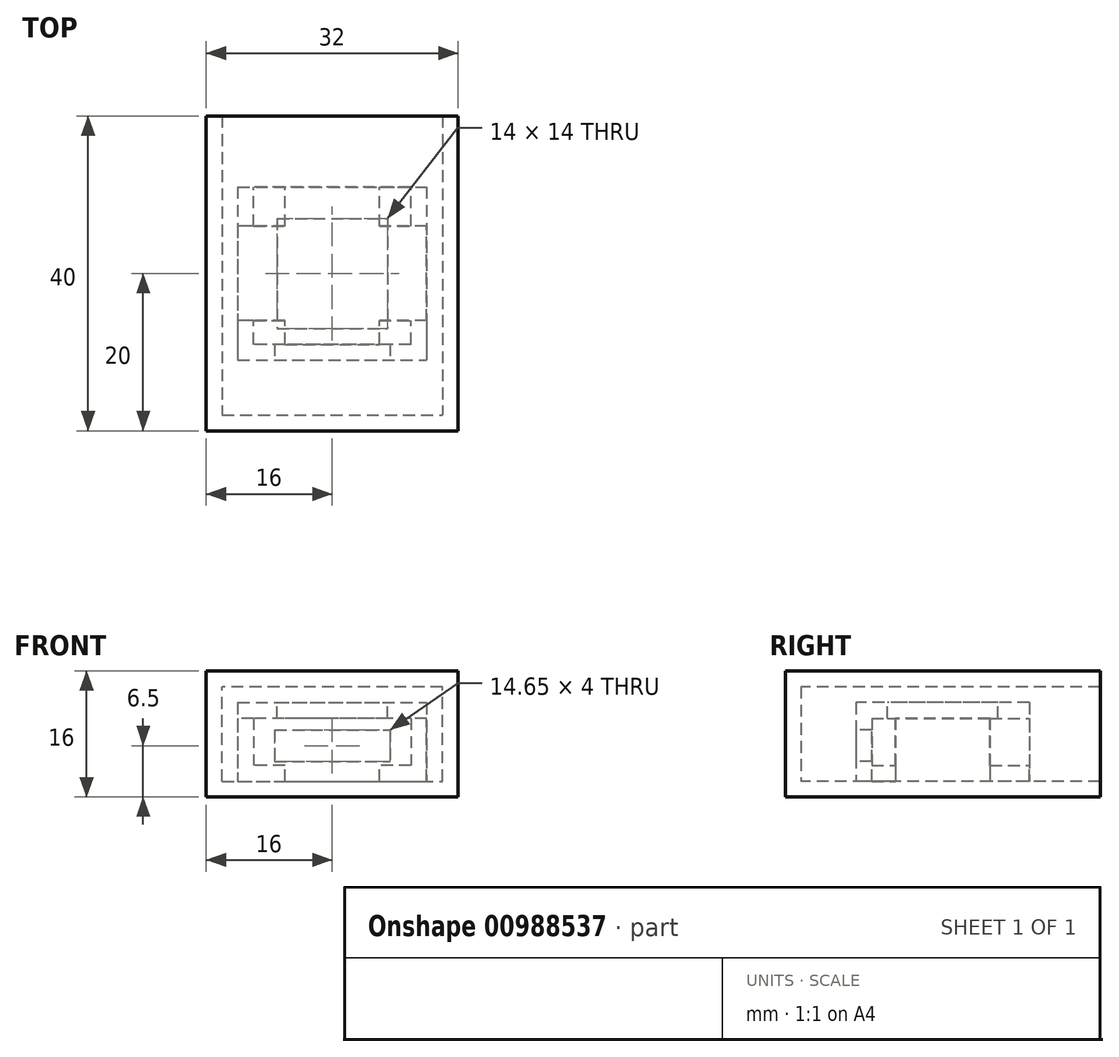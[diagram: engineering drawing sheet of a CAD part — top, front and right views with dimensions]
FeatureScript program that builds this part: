
annotation { "Feature Type Name" : "Feature", "Feature Type Description" : "" }
export const myFeature = defineFeature(function(context is Context, id is Id, definition is map)
    precondition{}
    {
        {
            var Q0;
            Q0=qCreatedBy(makeId("Top.planeOp"),FACE);
            var sketch = newSketch(context, id + "F0", { "sketchPlane" : qUnion([Q0])});
            skLineSegment(sketch, "E0.bottom", {"start": v(-16, 20) * mm, "end": v(16, 20) * mm});
            skLineSegment(sketch, "E0.top", {"start": v(-16, -20) * mm, "end": v(16, -20) * mm});
            skLineSegment(sketch, "E0.left", {"start": v(-16, 20) * mm, "end": v(-16, -20) * mm});
            skLineSegment(sketch, "E0.right", {"start": v(16, 20) * mm, "end": v(16, -20) * mm});
            skPoint(sketch, "E0.middle", {"position": v(0, 0) * mm});
            skSolve(sketch);
        }
        {
            var Q0;
            Q0=makeQuery(id+"F0.imprint","IMPRINT",FACE,{"disambiguationData":[TD([[makeQuery(id+"F0.imprint","IMPRINT",EDGE,{"derivedFrom":sQuery(id+"F0.wireOp",EDGE,"E0.bottom")}),-1.0]])]});
            extrude(context, id + "F1", {"entities" : qUnion([Q0]), "depth" : 2 * mm, "offsetDistance" : 25 * mm});
        }
        {
            var Q0;
            Q0=makeQuery(id+"F1.opExtrude","CAP_FACE",FACE,{"disambiguationData":[OSD([sQuery(id+"F0.wireOp",EDGE,"E0.bottom"),sQuery(id+"F0.wireOp",EDGE,"E0.top"),sQuery(id+"F0.wireOp",EDGE,"E0.left"),sQuery(id+"F0.wireOp",EDGE,"E0.right")])],"isStart":false});
            var sketch = newSketch(context, id + "F2", { "sketchPlane" : qUnion([Q0])});
            skLineSegment(sketch, "E1.bottom", {"start": v(-14, 18) * mm, "end": v(14, 18) * mm});
            skLineSegment(sketch, "E1.top", {"start": v(-14, -18) * mm, "end": v(14, -18) * mm});
            skLineSegment(sketch, "E1.left", {"start": v(-14, 18) * mm, "end": v(-14, -18) * mm});
            skLineSegment(sketch, "E1.right", {"start": v(14, 18) * mm, "end": v(14, -18) * mm});
            skPoint(sketch, "E1.middle", {"position": v(0, 0) * mm});
            skSolve(sketch);
        }
        {
            var Q0;
            Q0=makeQuery(id+"F2.imprint","IMPRINT",FACE,{"disambiguationData":[TD([[makeQuery(id+"F2.imprint","IMPRINT",EDGE,{"derivedFrom":sQuery(id+"F2.wireOp",EDGE,"E1.bottom")}),-1.0]])]});
            var sketch = newSketch(context, id + "F3", { "sketchPlane" : qUnion([Q0])});
            skLineSegment(sketch, "E2.bottom", {"start": v(-11, 11) * mm, "end": v(11, 11) * mm});
            skLineSegment(sketch, "E2.top", {"start": v(-11, -11) * mm, "end": v(11, -11) * mm});
            skLineSegment(sketch, "E2.left", {"start": v(-11, 11) * mm, "end": v(-11, -11) * mm});
            skLineSegment(sketch, "E2.right", {"start": v(11, 11) * mm, "end": v(11, -11) * mm});
            skPoint(sketch, "E2.middle", {"position": v(0, 0) * mm});
            skSolve(sketch);
        }
        {
            var Q0;
            Q0=makeQuery(id+"F3.imprint","IMPRINT",FACE,{"disambiguationData":[TD([[makeQuery(id+"F3.imprint","IMPRINT",EDGE,{"derivedFrom":sQuery(id+"F3.wireOp",EDGE,"E2.bottom")}),-1.0]])]});
            extrude(context, id + "F4", {"entities" : qUnion([Q0]), "operationType" : NewBodyOperationType.ADD, "depth" : 10 * mm, "offsetDistance" : 25 * mm});
        }
        {
            var Q0;
            Q0=makeQuery(id+"F4.opExtrude","SWEPT_FACE",FACE,{"disambiguationData":[OSD([sQuery(id+"F3.wireOp",EDGE,"E2.bottom")])]});
            var sketch = newSketch(context, id + "F5", { "sketchPlane" : qUnion([Q0])});
            skPoint(sketch, "E3", {"position": v(0, 7) * mm});
            skPoint(sketch, "E3.positionSnap0", {"position": v(0, 2) * mm});
            skLineSegment(sketch, "E4.bottom", {"start": v(-10, 10) * mm, "end": v(10, 10) * mm});
            skLineSegment(sketch, "E4.top", {"start": v(-10, 4) * mm, "end": v(10, 4) * mm});
            skLineSegment(sketch, "E4.left", {"start": v(-10, 10) * mm, "end": v(-10, 4) * mm});
            skLineSegment(sketch, "E4.right", {"start": v(10, 10) * mm, "end": v(10, 4) * mm});
            skSolve(sketch);
        }
        {
            var Q0;
            Q0=makeQuery(id+"F4.opExtrude","SWEPT_FACE",FACE,{"disambiguationData":[OSD([sQuery(id+"F3.wireOp",EDGE,"E2.left")])]});
            extrude(context, id + "F6", {"entities" : qUnion([Q0]), "operationType" : NewBodyOperationType.ADD, "depth" : 1 * mm, "offsetDistance" : 25 * mm});
        }
        {
            var Q0;
            Q0=makeQuery(id+"F4.opExtrude","SWEPT_FACE",FACE,{"disambiguationData":[OSD([sQuery(id+"F3.wireOp",EDGE,"E2.right")])]});
            extrude(context, id + "F7", {"entities" : qUnion([Q0]), "operationType" : NewBodyOperationType.ADD, "depth" : 1 * mm, "offsetDistance" : 25 * mm});
        }
        {
            var Q0;
            Q0=makeQuery(id+"F5.imprint","IMPRINT",FACE,{"disambiguationData":[TD([[makeQuery(id+"F5.imprint","IMPRINT",EDGE,{"derivedFrom":sQuery(id+"F5.wireOp",EDGE,"E4.bottom")}),-1.0]])]});
            extrude(context, id + "F8", {"entities" : qUnion([Q0]), "operationType" : NewBodyOperationType.REMOVE, "oppositeDirection" : true, "depth" : 20 * mm, "offsetDistance" : 25 * mm});
        }
        {
            var Q0;
            {var subQ0=sQuery(id+"F3.wireOp",EDGE,"E2.bottom");Q0=makeQuery(id+"F7.boolean.opBoolean","MERGE",FACE,{"derivedFrom":[makeQuery(id+"F6.boolean.opBoolean","MERGE",FACE,{"derivedFrom":[makeQuery(id+"F4.opExtrude","SWEPT_FACE",FACE,{"disambiguationData":[OSD([subQ0])]}),makeQuery(id+"F6.opExtrude","SWEPT_FACE",FACE,{"disambiguationData":[OSD([subQ0,sQuery(id+"F3.wireOp",EDGE,"E2.left")])]})]}),makeQuery(id+"F7.opExtrude","SWEPT_FACE",FACE,{"disambiguationData":[OSD([subQ0,sQuery(id+"F3.wireOp",EDGE,"E2.right")])]})]});}
            var sketch = newSketch(context, id + "F9", { "sketchPlane" : qUnion([Q0])});
            skPoint(sketch, "E5", {"position": v(0, 3) * mm});
            skPoint(sketch, "E5.positionSnap0", {"position": v(0, 2) * mm});
            skLineSegment(sketch, "E6.bottom", {"start": v(-6, 2) * mm, "end": v(6, 2) * mm});
            skLineSegment(sketch, "E6.top", {"start": v(-6, 4) * mm, "end": v(6, 4) * mm});
            skLineSegment(sketch, "E6.left", {"start": v(-6, 2) * mm, "end": v(-6, 4) * mm});
            skLineSegment(sketch, "E6.right", {"start": v(6, 2) * mm, "end": v(6, 4) * mm});
            skSolve(sketch);
        }
        {
            var Q0;
            Q0=makeQuery(id+"F9.imprint","IMPRINT",FACE,{"disambiguationData":[TD([[makeQuery(id+"F9.imprint","IMPRINT",EDGE,{"derivedFrom":sQuery(id+"F9.wireOp",EDGE,"E6.bottom")}),-1.0]])]});
            extrude(context, id + "F10", {"entities" : qUnion([Q0]), "operationType" : NewBodyOperationType.REMOVE, "oppositeDirection" : true, "depth" : 20 * mm, "offsetDistance" : 25 * mm});
        }
        {
            var Q0;
            Q0=makeQuery(id+"F6.opExtrude","CAP_FACE",FACE,{"disambiguationData":[OSD([sQuery(id+"F3.wireOp",EDGE,"E2.left")])],"isStart":false});
            var sketch = newSketch(context, id + "F11", { "sketchPlane" : qUnion([Q0])});
            skPoint(sketch, "E7", {"position": v(0, 6) * mm});
            skPoint(sketch, "E7.positionSnap0", {"position": v(0, 2) * mm});
            skLineSegment(sketch, "E8.bottom", {"start": v(-6, 10) * mm, "end": v(6, 10) * mm});
            skLineSegment(sketch, "E8.top", {"start": v(-6, 2) * mm, "end": v(6, 2) * mm});
            skLineSegment(sketch, "E8.left", {"start": v(-6, 10) * mm, "end": v(-6, 2) * mm});
            skLineSegment(sketch, "E8.right", {"start": v(6, 10) * mm, "end": v(6, 2) * mm});
            skSolve(sketch);
        }
        {
            var Q0;
            Q0=makeQuery(id+"F11.imprint","IMPRINT",FACE,{"disambiguationData":[TD([[makeQuery(id+"F11.imprint","IMPRINT",EDGE,{"derivedFrom":sQuery(id+"F11.wireOp",EDGE,"E8.bottom")}),-1.0]])]});
            extrude(context, id + "F12", {"entities" : qUnion([Q0]), "operationType" : NewBodyOperationType.REMOVE, "oppositeDirection" : true, "depth" : 25 * mm, "offsetDistance" : 25 * mm});
        }
        {
            var Q0;
            {var subQ0=sQuery(id+"F3.wireOp",EDGE,"E2.top");Q0=makeQuery(id+"F7.boolean.opBoolean","MERGE",FACE,{"derivedFrom":[makeQuery(id+"F6.boolean.opBoolean","MERGE",FACE,{"derivedFrom":[makeQuery(id+"F4.opExtrude","SWEPT_FACE",FACE,{"disambiguationData":[OSD([subQ0])]}),makeQuery(id+"F6.opExtrude","SWEPT_FACE",FACE,{"disambiguationData":[OSD([subQ0,sQuery(id+"F3.wireOp",EDGE,"E2.left")])]})]}),makeQuery(id+"F7.opExtrude","SWEPT_FACE",FACE,{"disambiguationData":[OSD([subQ0,sQuery(id+"F3.wireOp",EDGE,"E2.right")])]})]});}
            var sketch = newSketch(context, id + "F13", { "sketchPlane" : qUnion([Q0])});
            skPoint(sketch, "E9", {"position": v(0, 6.5) * mm});
            skPoint(sketch, "E9.positionSnap0", {"position": v(0, 2) * mm});
            skLineSegment(sketch, "E10.bottom", {"start": v(-7.32, 8.5) * mm, "end": v(7.32, 8.5) * mm});
            skLineSegment(sketch, "E10.top", {"start": v(-7.32, 4.5) * mm, "end": v(7.32, 4.5) * mm});
            skLineSegment(sketch, "E10.left", {"start": v(-7.32, 8.5) * mm, "end": v(-7.32, 4.5) * mm});
            skLineSegment(sketch, "E10.right", {"start": v(7.32, 8.5) * mm, "end": v(7.32, 4.5) * mm});
            skSolve(sketch);
        }
        {
            var Q0;
            Q0=makeQuery(id+"F13.imprint","IMPRINT",FACE,{"disambiguationData":[TD([[makeQuery(id+"F13.imprint","IMPRINT",EDGE,{"derivedFrom":sQuery(id+"F13.wireOp",EDGE,"E10.bottom")}),-1.0]])]});
            extrude(context, id + "F14", {"entities" : qUnion([Q0]), "operationType" : NewBodyOperationType.REMOVE, "oppositeDirection" : true, "depth" : 25 * mm, "offsetDistance" : 25 * mm});
        }
        {
            var Q0;
            {var subQ0=sQuery(id+"F3.wireOp",EDGE,"E2.right");var subQ1=sQuery(id+"F3.wireOp",EDGE,"E2.left");Q0=makeQuery(id+"F7.boolean.opBoolean","MERGE",FACE,{"derivedFrom":[makeQuery(id+"F6.boolean.opBoolean","MERGE",FACE,{"derivedFrom":[makeQuery(id+"F4.opExtrude","CAP_FACE",FACE,{"disambiguationData":[OSD([sQuery(id+"F3.wireOp",EDGE,"E2.bottom"),sQuery(id+"F3.wireOp",EDGE,"E2.top"),subQ1,subQ0])],"isStart":false}),makeQuery(id+"F6.opExtrude","SWEPT_FACE",FACE,{"disambiguationData":[OSD([subQ1]),TDD([makeQuery(id+"F4.opExtrude","CAP_EDGE",EDGE,{"disambiguationData":[OSD([subQ1])],"isStart":false})])]})]}),makeQuery(id+"F7.opExtrude","SWEPT_FACE",FACE,{"disambiguationData":[OSD([subQ0]),TDD([makeQuery(id+"F4.opExtrude","CAP_EDGE",EDGE,{"disambiguationData":[OSD([subQ0])],"isStart":false})])]})]});}
            var sketch = newSketch(context, id + "F15", { "sketchPlane" : qUnion([Q0])});
            skLineSegment(sketch, "E11.bottom", {"start": v(-7, 7) * mm, "end": v(7, 7) * mm});
            skLineSegment(sketch, "E11.top", {"start": v(-7, -7) * mm, "end": v(7, -7) * mm});
            skLineSegment(sketch, "E11.left", {"start": v(-7, 7) * mm, "end": v(-7, -7) * mm});
            skLineSegment(sketch, "E11.right", {"start": v(7, 7) * mm, "end": v(7, -7) * mm});
            skPoint(sketch, "E11.middle", {"position": v(0, 0) * mm});
            skSolve(sketch);
        }
        {
            var Q0;
            Q0=makeQuery(id+"F15.imprint","IMPRINT",FACE,{"disambiguationData":[TD([[makeQuery(id+"F15.imprint","IMPRINT",EDGE,{"derivedFrom":sQuery(id+"F15.wireOp",EDGE,"E11.bottom")}),-1.0]])]});
            extrude(context, id + "F16", {"entities" : qUnion([Q0]), "operationType" : NewBodyOperationType.REMOVE, "oppositeDirection" : true, "depth" : 5 * mm, "offsetDistance" : 25 * mm});
        }
        {
            var Q0;
            Q0=makeQuery(id+"F2.imprint","IMPRINT",FACE,{"disambiguationData":[TD([[makeQuery(id+"F2.imprint","IMPRINT",EDGE,{"derivedFrom":sQuery(id+"F2.wireOp",EDGE,"E1.bottom")}),1.0]])]});
            extrude(context, id + "F17", {"entities" : qUnion([Q0]), "operationType" : NewBodyOperationType.ADD, "depth" : 14 * mm, "offsetDistance" : 25 * mm});
        }
        {
            var Q0;
            Q0=makeQuery(id+"F17.opExtrude","SWEPT_FACE",FACE,{"disambiguationData":[OSD([sQuery(id+"F2.wireOp",EDGE,"E1.top")])]});
            var sketch = newSketch(context, id + "F18", { "sketchPlane" : qUnion([Q0])});
            skPoint(sketch, "E12", {"position": v(0, 16) * mm});
            skPoint(sketch, "E13", {"position": v(-14, 16) * mm});
            skPoint(sketch, "E14", {"position": v(0, 15) * mm});
            skLineSegment(sketch, "E15.bottom", {"start": v(-14, 14) * mm, "end": v(14, 14) * mm});
            skLineSegment(sketch, "E15.top", {"start": v(-14, 16) * mm, "end": v(14, 16) * mm});
            skLineSegment(sketch, "E15.left", {"start": v(-14, 14) * mm, "end": v(-14, 16) * mm});
            skLineSegment(sketch, "E15.right", {"start": v(14, 14) * mm, "end": v(14, 16) * mm});
            skSolve(sketch);
        }
        {
            var Q0;
            Q0=makeQuery(id+"F17.opExtrude","CAP_FACE",FACE,{"disambiguationData":[OSD([sQuery(id+"F0.wireOp",EDGE,"E0.bottom"),sQuery(id+"F0.wireOp",EDGE,"E0.top"),sQuery(id+"F0.wireOp",EDGE,"E0.left"),sQuery(id+"F0.wireOp",EDGE,"E0.right"),sQuery(id+"F2.wireOp",EDGE,"E1.bottom"),sQuery(id+"F2.wireOp",EDGE,"E1.top"),sQuery(id+"F2.wireOp",EDGE,"E1.left"),sQuery(id+"F2.wireOp",EDGE,"E1.right")])],"isStart":false});
            var sketch = newSketch(context, id + "F19", { "sketchPlane" : qUnion([Q0])});
            skPoint(sketch, "E16", {"position": v(-14, 18) * mm});
            skPoint(sketch, "E17", {"position": v(0, 18) * mm});
            skPoint(sketch, "E18", {"position": v(0, 19) * mm});
            skLineSegment(sketch, "E19.bottom", {"start": v(-14, 20) * mm, "end": v(14, 20) * mm});
            skLineSegment(sketch, "E19.top", {"start": v(-14, 18) * mm, "end": v(14, 18) * mm});
            skLineSegment(sketch, "E19.left", {"start": v(-14, 20) * mm, "end": v(-14, 18) * mm});
            skLineSegment(sketch, "E19.right", {"start": v(14, 20) * mm, "end": v(14, 18) * mm});
            skSolve(sketch);
        }
        {
            var Q0;
            Q0=makeQuery(id+"F19.imprint","IMPRINT",FACE,{"disambiguationData":[TD([[makeQuery(id+"F19.imprint","IMPRINT",EDGE,{"derivedFrom":sQuery(id+"F19.wireOp",EDGE,"E19.bottom")}),-1.0]])]});
            extrude(context, id + "F20", {"entities" : qUnion([Q0]), "operationType" : NewBodyOperationType.REMOVE, "oppositeDirection" : true, "depth" : 14 * mm, "offsetDistance" : 25 * mm});
        }
        {
            var Q0;
            Q0=makeQuery(id+"F18.imprint","IMPRINT",FACE,{"disambiguationData":[TD([[makeQuery(id+"F18.imprint","IMPRINT",EDGE,{"derivedFrom":sQuery(id+"F18.wireOp",EDGE,"E15.bottom")}),1.0]])]});
            extrude(context, id + "F21", {"entities" : qUnion([Q0]), "operationType" : NewBodyOperationType.ADD, "depth" : 38 * mm, "offsetDistance" : 25 * mm});
        }
    });
